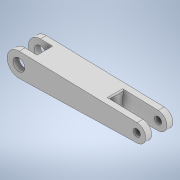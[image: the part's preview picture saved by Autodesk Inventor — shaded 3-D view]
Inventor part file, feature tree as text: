
AUTODESK INVENTOR PART (.ipt)
format: ipt  version: 2021 (Build 250183000, 183)  size: 152,064 bytes
history: native  units: in
note: dims shown in document units (in); Inventor stores cm internally (conversion verified against a paired STEP export)
features: extrude x2, fillet x2, sketch x2
ambient origin geometry x8: Origin, YZ Plane, XZ Plane, XY Plane, X Axis, Y Axis, Z Axis, Center Point
bodies: Solid1 (feature_tree)
feature tree (6):
  extrude  "Extrusion1"  Depth=0.0787in
  extrude  "Extrusion2"  Depth=0.0079in
  fillet  "Fillet1"  Radius=0.0472in
  fillet  "Fillet2"  Radius=0.1811in
  sketch  "Sketch1"  dims[d0=0.1575in d1=0.0787in]
  sketch  "Sketch2"  dims[d2=0.7874in d3=0.1181in d4=0.0472in d5=0.1811in d6=0.0in d7=0.0787in d8=0.1969in d10=0.4724in d11=0.1024in d12=0.0in d13=0.0039in d14=0.0079in d9=0.0197in]
